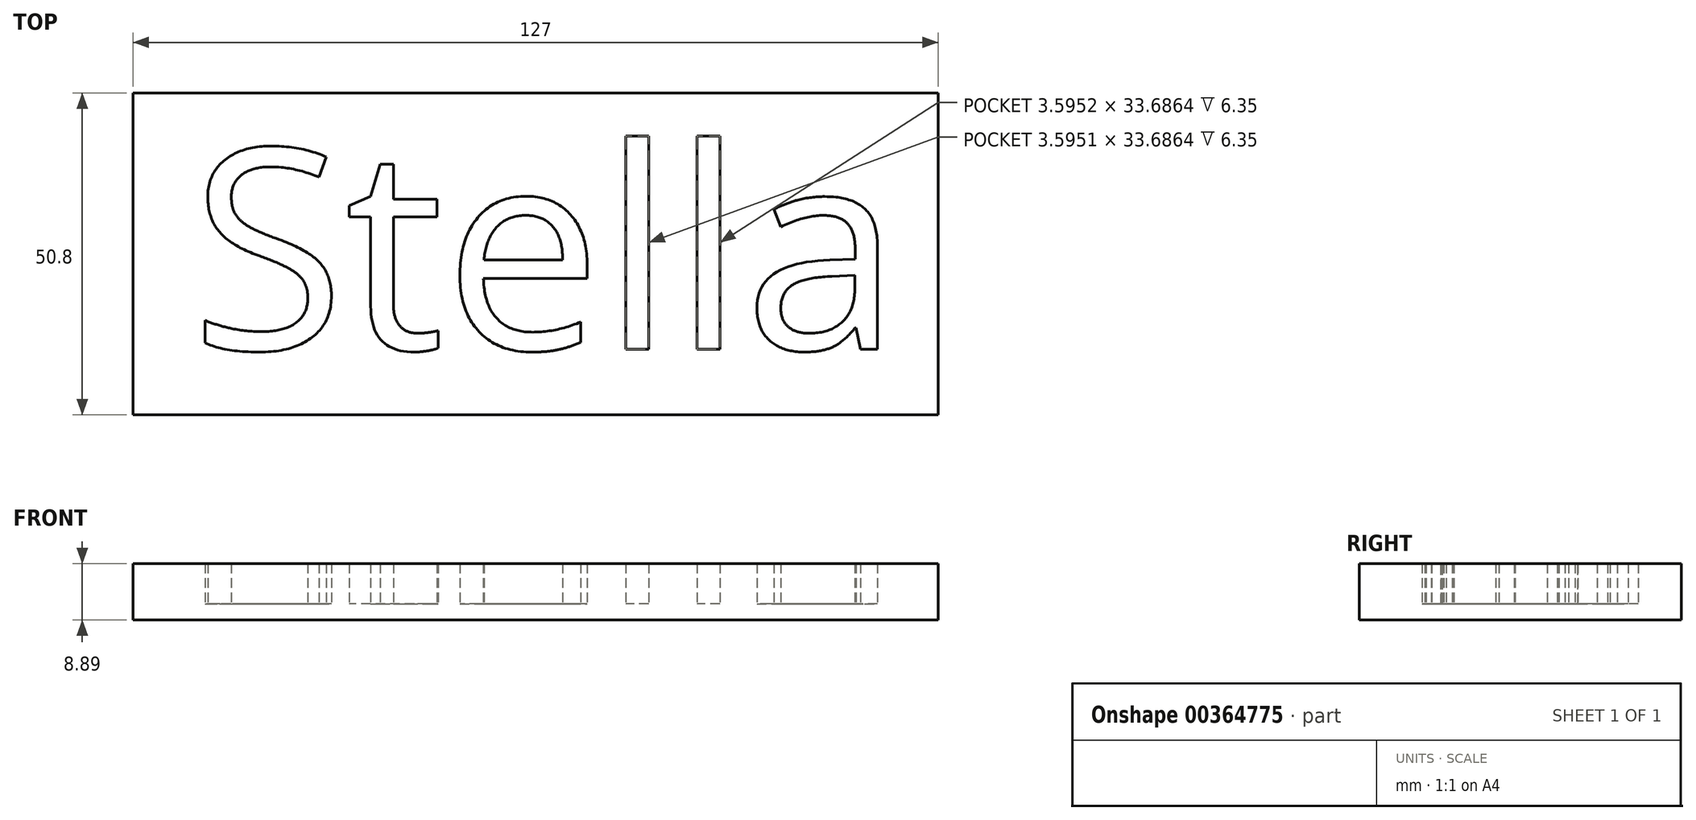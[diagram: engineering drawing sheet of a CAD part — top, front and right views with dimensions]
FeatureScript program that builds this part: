
annotation { "Feature Type Name" : "Feature", "Feature Type Description" : "" }
export const myFeature = defineFeature(function(context is Context, id is Id, definition is map)
    precondition{}
    {
        {
            var Q0;
            Q0=qCreatedBy(makeId("Top.planeOp"),FACE);
            var sketch = newSketch(context, id + "F0", { "sketchPlane" : qUnion([Q0])});
            skLineSegment(sketch, "E0.bottom", {"start": v(-72.82, 19.12) * mm, "end": v(54.18, 19.12) * mm});
            skLineSegment(sketch, "E0.top", {"start": v(-72.82, -31.68) * mm, "end": v(54.18, -31.68) * mm});
            skLineSegment(sketch, "E0.left", {"start": v(-72.82, 19.12) * mm, "end": v(-72.82, -31.68) * mm});
            skLineSegment(sketch, "E0.right", {"start": v(54.18, 19.12) * mm, "end": v(54.18, -31.68) * mm});
            skText(sketch, "E1", { "text": "Stella\n", "fontName": "OpenSans-Regular.ttf"});
            const initialGuessF0  = {"E1": [-0.06373, -0.02135, 1, 0, 0.03192]};
            skSetInitialGuess(sketch, initialGuessF0);
            skSolve(sketch);
        }
        {
            var Q0;
            Q0=makeQuery(id+"F0.imprint","IMPRINT",FACE,{"disambiguationData":[TD([[makeQuery(id+"F0.imprint","IMPRINT",EDGE,{"derivedFrom":sQuery(id+"F0.wireOp",EDGE,"E0.bottom")}),-1.0]])]});
            var Q1;
            Q1=makeQuery(id+"F0.imprint","IMPRINT",FACE,{"disambiguationData":[TD([[makeQuery(id+"F0.imprint","IMPRINT",EDGE,{"derivedFrom":sQuery(id+"F0.wireOp",EDGE,"E1.sketch_text.stroke-58")}),1.0]])]});
            var Q2;
            Q2=makeQuery(id+"F0.imprint","IMPRINT",FACE,{"disambiguationData":[TD([[makeQuery(id+"F0.imprint","IMPRINT",EDGE,{"derivedFrom":sQuery(id+"F0.wireOp",EDGE,"E1.sketch_text.stroke-90")}),1.0]])]});
            extrude(context, id + "F1", {"entities" : qUnion([Q0, Q1, Q2]), "depth" : 6.35 * mm});
        }
        {
            var Q0;
            Q0=makeQuery(id+"F1.opExtrude","CAP_FACE",FACE,{"disambiguationData":[OSD([sQuery(id+"F0.wireOp",EDGE,"E0.bottom"),sQuery(id+"F0.wireOp",EDGE,"E0.top"),sQuery(id+"F0.wireOp",EDGE,"E0.left"),sQuery(id+"F0.wireOp",EDGE,"E0.right"),sQuery(id+"F0.wireOp",EDGE,"E1.sketch_text.stroke-0"),sQuery(id+"F0.wireOp",EDGE,"E1.sketch_text.stroke-1"),sQuery(id+"F0.wireOp",EDGE,"E1.sketch_text.stroke-2"),sQuery(id+"F0.wireOp",EDGE,"E1.sketch_text.stroke-3"),sQuery(id+"F0.wireOp",EDGE,"E1.sketch_text.stroke-4"),sQuery(id+"F0.wireOp",EDGE,"E1.sketch_text.stroke-5"),sQuery(id+"F0.wireOp",EDGE,"E1.sketch_text.stroke-6"),sQuery(id+"F0.wireOp",EDGE,"E1.sketch_text.stroke-7"),sQuery(id+"F0.wireOp",EDGE,"E1.sketch_text.stroke-8"),sQuery(id+"F0.wireOp",EDGE,"E1.sketch_text.stroke-9"),sQuery(id+"F0.wireOp",EDGE,"E1.sketch_text.stroke-10"),sQuery(id+"F0.wireOp",EDGE,"E1.sketch_text.stroke-11"),sQuery(id+"F0.wireOp",EDGE,"E1.sketch_text.stroke-12"),sQuery(id+"F0.wireOp",EDGE,"E1.sketch_text.stroke-13"),sQuery(id+"F0.wireOp",EDGE,"E1.sketch_text.stroke-14"),sQuery(id+"F0.wireOp",EDGE,"E1.sketch_text.stroke-15"),sQuery(id+"F0.wireOp",EDGE,"E1.sketch_text.stroke-16"),sQuery(id+"F0.wireOp",EDGE,"E1.sketch_text.stroke-17"),sQuery(id+"F0.wireOp",EDGE,"E1.sketch_text.stroke-18"),sQuery(id+"F0.wireOp",EDGE,"E1.sketch_text.stroke-19"),sQuery(id+"F0.wireOp",EDGE,"E1.sketch_text.stroke-20"),sQuery(id+"F0.wireOp",EDGE,"E1.sketch_text.stroke-21"),sQuery(id+"F0.wireOp",EDGE,"E1.sketch_text.stroke-22"),sQuery(id+"F0.wireOp",EDGE,"E1.sketch_text.stroke-23"),sQuery(id+"F0.wireOp",EDGE,"E1.sketch_text.stroke-24"),sQuery(id+"F0.wireOp",EDGE,"E1.sketch_text.stroke-25"),sQuery(id+"F0.wireOp",EDGE,"E1.sketch_text.stroke-26"),sQuery(id+"F0.wireOp",EDGE,"E1.sketch_text.stroke-27"),sQuery(id+"F0.wireOp",EDGE,"E1.sketch_text.stroke-28"),sQuery(id+"F0.wireOp",EDGE,"E1.sketch_text.stroke-29"),sQuery(id+"F0.wireOp",EDGE,"E1.sketch_text.stroke-30"),sQuery(id+"F0.wireOp",EDGE,"E1.sketch_text.stroke-31"),sQuery(id+"F0.wireOp",EDGE,"E1.sketch_text.stroke-32"),sQuery(id+"F0.wireOp",EDGE,"E1.sketch_text.stroke-33"),sQuery(id+"F0.wireOp",EDGE,"E1.sketch_text.stroke-34"),sQuery(id+"F0.wireOp",EDGE,"E1.sketch_text.stroke-35"),sQuery(id+"F0.wireOp",EDGE,"E1.sketch_text.stroke-36"),sQuery(id+"F0.wireOp",EDGE,"E1.sketch_text.stroke-37"),sQuery(id+"F0.wireOp",EDGE,"E1.sketch_text.stroke-38"),sQuery(id+"F0.wireOp",EDGE,"E1.sketch_text.stroke-39"),sQuery(id+"F0.wireOp",EDGE,"E1.sketch_text.stroke-40"),sQuery(id+"F0.wireOp",EDGE,"E1.sketch_text.stroke-41"),sQuery(id+"F0.wireOp",EDGE,"E1.sketch_text.stroke-42"),sQuery(id+"F0.wireOp",EDGE,"E1.sketch_text.stroke-43"),sQuery(id+"F0.wireOp",EDGE,"E1.sketch_text.stroke-44"),sQuery(id+"F0.wireOp",EDGE,"E1.sketch_text.stroke-45"),sQuery(id+"F0.wireOp",EDGE,"E1.sketch_text.stroke-46"),sQuery(id+"F0.wireOp",EDGE,"E1.sketch_text.stroke-47"),sQuery(id+"F0.wireOp",EDGE,"E1.sketch_text.stroke-48"),sQuery(id+"F0.wireOp",EDGE,"E1.sketch_text.stroke-49"),sQuery(id+"F0.wireOp",EDGE,"E1.sketch_text.stroke-50"),sQuery(id+"F0.wireOp",EDGE,"E1.sketch_text.stroke-51"),sQuery(id+"F0.wireOp",EDGE,"E1.sketch_text.stroke-52"),sQuery(id+"F0.wireOp",EDGE,"E1.sketch_text.stroke-53"),sQuery(id+"F0.wireOp",EDGE,"E1.sketch_text.stroke-54"),sQuery(id+"F0.wireOp",EDGE,"E1.sketch_text.stroke-55"),sQuery(id+"F0.wireOp",EDGE,"E1.sketch_text.stroke-56"),sQuery(id+"F0.wireOp",EDGE,"E1.sketch_text.stroke-57"),sQuery(id+"F0.wireOp",EDGE,"E1.sketch_text.stroke-63"),sQuery(id+"F0.wireOp",EDGE,"E1.sketch_text.stroke-64"),sQuery(id+"F0.wireOp",EDGE,"E1.sketch_text.stroke-65"),sQuery(id+"F0.wireOp",EDGE,"E1.sketch_text.stroke-66"),sQuery(id+"F0.wireOp",EDGE,"E1.sketch_text.stroke-67"),sQuery(id+"F0.wireOp",EDGE,"E1.sketch_text.stroke-68"),sQuery(id+"F0.wireOp",EDGE,"E1.sketch_text.stroke-69"),sQuery(id+"F0.wireOp",EDGE,"E1.sketch_text.stroke-70"),sQuery(id+"F0.wireOp",EDGE,"E1.sketch_text.stroke-71"),sQuery(id+"F0.wireOp",EDGE,"E1.sketch_text.stroke-72"),sQuery(id+"F0.wireOp",EDGE,"E1.sketch_text.stroke-73"),sQuery(id+"F0.wireOp",EDGE,"E1.sketch_text.stroke-74"),sQuery(id+"F0.wireOp",EDGE,"E1.sketch_text.stroke-75"),sQuery(id+"F0.wireOp",EDGE,"E1.sketch_text.stroke-76"),sQuery(id+"F0.wireOp",EDGE,"E1.sketch_text.stroke-77"),sQuery(id+"F0.wireOp",EDGE,"E1.sketch_text.stroke-78"),sQuery(id+"F0.wireOp",EDGE,"E1.sketch_text.stroke-79"),sQuery(id+"F0.wireOp",EDGE,"E1.sketch_text.stroke-80"),sQuery(id+"F0.wireOp",EDGE,"E1.sketch_text.stroke-81"),sQuery(id+"F0.wireOp",EDGE,"E1.sketch_text.stroke-82"),sQuery(id+"F0.wireOp",EDGE,"E1.sketch_text.stroke-83"),sQuery(id+"F0.wireOp",EDGE,"E1.sketch_text.stroke-84"),sQuery(id+"F0.wireOp",EDGE,"E1.sketch_text.stroke-85"),sQuery(id+"F0.wireOp",EDGE,"E1.sketch_text.stroke-86"),sQuery(id+"F0.wireOp",EDGE,"E1.sketch_text.stroke-87"),sQuery(id+"F0.wireOp",EDGE,"E1.sketch_text.stroke-88"),sQuery(id+"F0.wireOp",EDGE,"E1.sketch_text.stroke-89")])],"isStart":true});
            var sketch = newSketch(context, id + "F2", { "sketchPlane" : qUnion([Q0])});
            skLineSegment(sketch, "E2.bottom", {"start": v(-72.82, 31.68) * mm, "end": v(54.18, 31.68) * mm});
            skLineSegment(sketch, "E2.top", {"start": v(-72.82, -19.12) * mm, "end": v(54.18, -19.12) * mm});
            skLineSegment(sketch, "E2.left", {"start": v(-72.82, 31.68) * mm, "end": v(-72.82, -19.12) * mm});
            skLineSegment(sketch, "E2.right", {"start": v(54.18, 31.68) * mm, "end": v(54.18, -19.12) * mm});
            skSolve(sketch);
        }
        {
            var Q0;
            Q0 = qSketchRegion(id + "F2", true);
            extrude(context, id + "F3", {"entities" : qUnion([Q0]), "operationType" : NewBodyOperationType.ADD, "depth" : 2.54 * mm});
        }
    });
